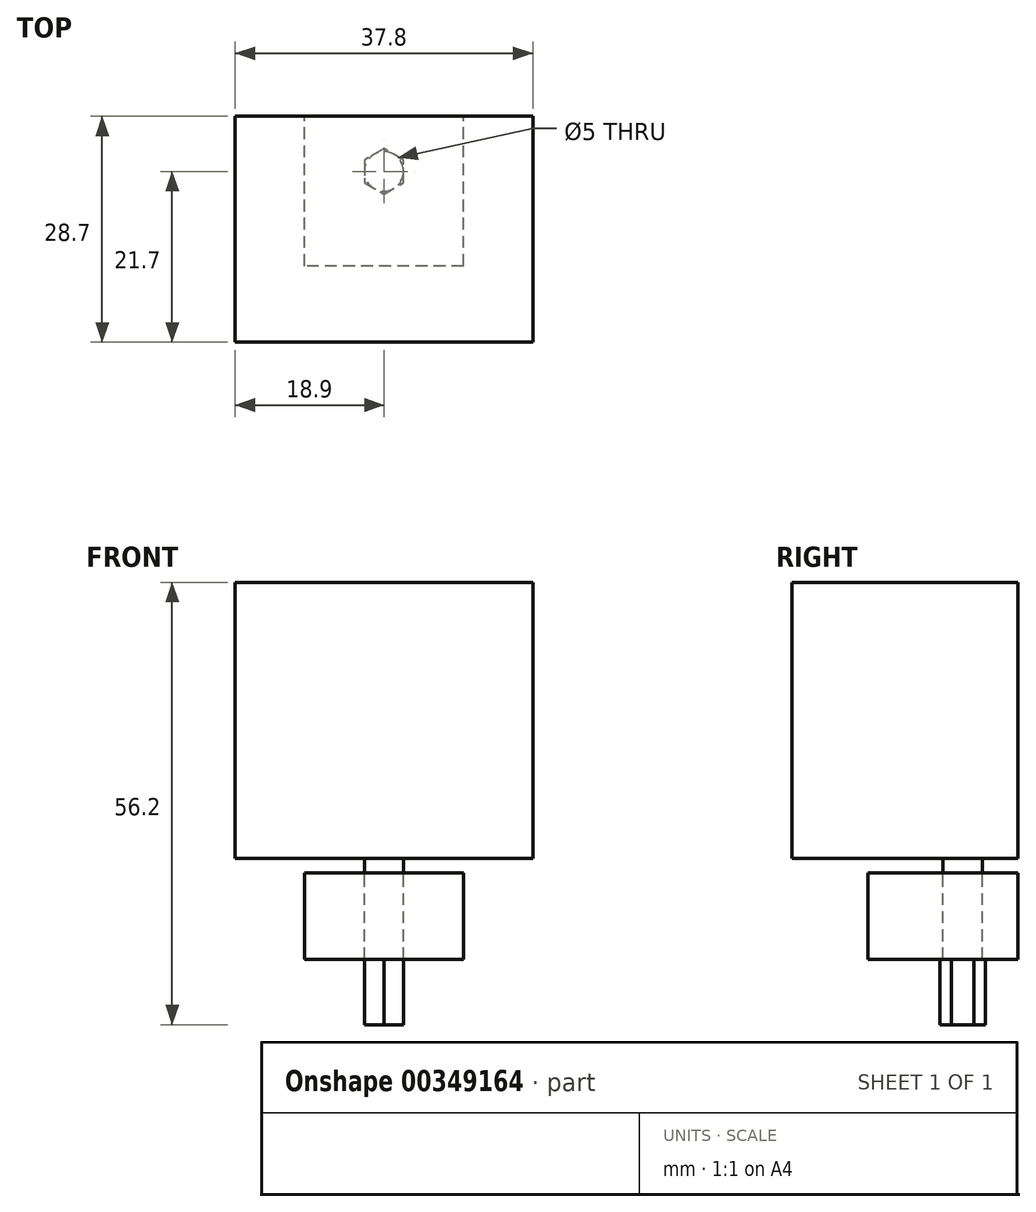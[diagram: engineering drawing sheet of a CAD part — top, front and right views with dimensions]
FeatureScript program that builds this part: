
annotation { "Feature Type Name" : "Feature", "Feature Type Description" : "" }
export const myFeature = defineFeature(function(context is Context, id is Id, definition is map)
    precondition{}
    {
        {
            var Q0;
            Q0=qCreatedBy(makeId("Top.planeOp"),FACE);
            var sketch = newSketch(context, id + "F0", { "sketchPlane" : qUnion([Q0])});
            skLineSegment(sketch, "E0.bottom", {"start": v(18.9, 14.35) * mm, "end": v(-18.9, 14.35) * mm});
            skLineSegment(sketch, "E0.top", {"start": v(18.9, -14.35) * mm, "end": v(-18.9, -14.35) * mm});
            skLineSegment(sketch, "E0.left", {"start": v(18.9, 14.35) * mm, "end": v(18.9, -14.35) * mm});
            skLineSegment(sketch, "E0.right", {"start": v(-18.9, 14.35) * mm, "end": v(-18.9, -14.35) * mm});
            skPoint(sketch, "E0.middle", {"position": v(0, 0) * mm});
            skSolve(sketch);
        }
        {
            var Q0;
            Q0 = qSketchRegion(id + "F0", true);
            extrude(context, id + "F1", {"entities" : qUnion([Q0]), "depth" : 35.1 * mm, "offsetDistance" : 25.4 * mm});
        }
        {
            var Q0;
            Q0=makeQuery(id+"F1.opExtrude","CAP_FACE",FACE,{"disambiguationData":[OSD([sQuery(id+"F0.wireOp",EDGE,"E0.bottom"),sQuery(id+"F0.wireOp",EDGE,"E0.top"),sQuery(id+"F0.wireOp",EDGE,"E0.left"),sQuery(id+"F0.wireOp",EDGE,"E0.right")])],"isStart":true});
            var sketch = newSketch(context, id + "F2", { "sketchPlane" : qUnion([Q0])});
            skCircle(sketch, "E1", {"center": v(0, -7.35) * mm, "radius": 2.5 * mm});
            skSolve(sketch);
        }
        {
            var Q0;
            Q0 = qSketchRegion(id + "F2", true);
            extrude(context, id + "F3", {"entities" : qUnion([Q0]), "operationType" : NewBodyOperationType.ADD, "depth" : 1.8 * mm, "offsetDistance" : 25 * mm});
        }
        {
            var Q0;
            Q0=makeQuery(id+"F3.opExtrude","CAP_FACE",FACE,{"disambiguationData":[OSD([sQuery(id+"F2.wireOp",EDGE,"E1")])],"isStart":false});
            var sketch = newSketch(context, id + "F4", { "sketchPlane" : qUnion([Q0])});
            skLineSegment(sketch, "E2.bottom", {"start": v(10.1, 4.65) * mm, "end": v(-10.1, 4.65) * mm});
            skLineSegment(sketch, "E2.top", {"start": v(10.1, -14.35) * mm, "end": v(-10.1, -14.35) * mm});
            skLineSegment(sketch, "E2.left", {"start": v(10.1, 4.65) * mm, "end": v(10.1, -14.35) * mm});
            skLineSegment(sketch, "E2.right", {"start": v(-10.1, 4.65) * mm, "end": v(-10.1, -14.35) * mm});
            skLineSegment(sketch, "E3", {"start": v(10.1, -7.35) * mm, "end": v(-10.1, -7.35) * mm, "construction": true});
            skCircle(sketch, "E4.0", {"center": v(0, -7.35) * mm, "radius": 2.5 * mm});
            skSolve(sketch);
        }
        {
            var Q0;
            Q0=makeQuery(id+"F4.imprint","IMPRINT",FACE,{"disambiguationData":[TD([[makeQuery(id+"F4.imprint","IMPRINT",EDGE,{"derivedFrom":sQuery(id+"F4.wireOp",EDGE,"E2.bottom")}),1.0]])]});
            extrude(context, id + "F5", {"entities" : qUnion([Q0]), "depth" : 11 * mm, "offsetDistance" : 25 * mm});
        }
        {
            var Q0;
            Q0=makeQuery(id+"F5.opExtrude","CAP_FACE",FACE,{"disambiguationData":[OSD([sQuery(id+"F4.wireOp",EDGE,"E2.bottom"),sQuery(id+"F4.wireOp",EDGE,"E2.top"),sQuery(id+"F4.wireOp",EDGE,"E2.left"),sQuery(id+"F4.wireOp",EDGE,"E2.right"),sQuery(id+"F4.wireOp",EDGE,"E4.0")])],"isStart":false});
            var sketch = newSketch(context, id + "F6", { "sketchPlane" : qUnion([Q0])});
            skCircle(sketch, "E5.0", {"center": v(0, -7.35) * mm, "radius": 2.5 * mm});
            skCircle(sketch, "E6.cCircle", {"center": v(0, -7.35) * mm, "radius": 2.5 * mm, "construction": true});
            skLineSegment(sketch, "E6.0", {"start": v(2.5, -5.9) * mm, "end": v(2.5, -8.8) * mm});
            skLineSegment(sketch, "E6.1", {"start": v(2.5, -8.8) * mm, "end": v(0, -10.24) * mm});
            skLineSegment(sketch, "E6.2", {"start": v(0, -10.24) * mm, "end": v(-2.5, -8.8) * mm});
            skLineSegment(sketch, "E6.3", {"start": v(-2.5, -8.8) * mm, "end": v(-2.5, -5.9) * mm});
            skLineSegment(sketch, "E6.4", {"start": v(-2.5, -5.9) * mm, "end": v(0, -4.46) * mm});
            skLineSegment(sketch, "E6.5", {"start": v(0, -4.46) * mm, "end": v(2.5, -5.9) * mm});
            skPoint(sketch, "E6.0.midPoint", {"position": v(2.5, -7.35) * mm});
            skSolve(sketch);
        }
        {
            var Q0;
            {var subQ0=sQuery(id+"F6.wireOp",EDGE,"E6.2");var subQ1=sQuery(id+"F6.wireOp",EDGE,"E5.0");var subQ2=makeQuery(id+"F6.imprint","INTERSECT",VERTEX,{"derivedFrom":[subQ1,subQ0]});Q0=makeQuery(id+"F6.imprint","IMPRINT",FACE,{"disambiguationData":[TD([[makeQuery(id+"F6.imprint","IMPRINT",EDGE,{"disambiguationData":[TD([[subQ2,-1.0]])],"derivedFrom":subQ1}),-1.0]])]});}
            var Q1;
            {var subQ0=sQuery(id+"F6.wireOp",EDGE,"E6.0");var subQ1=sQuery(id+"F6.wireOp",EDGE,"E5.0");var subQ2=makeQuery(id+"F6.imprint","INTERSECT",VERTEX,{"derivedFrom":[subQ1,subQ0]});Q1=makeQuery(id+"F6.imprint","IMPRINT",FACE,{"disambiguationData":[TD([[makeQuery(id+"F6.imprint","IMPRINT",EDGE,{"disambiguationData":[TD([[subQ2,1.0]])],"derivedFrom":subQ1}),-1.0]])]});}
            var Q2;
            {var subQ0=sQuery(id+"F6.wireOp",EDGE,"E6.3");var subQ1=sQuery(id+"F6.wireOp",EDGE,"E5.0");var subQ2=makeQuery(id+"F6.imprint","INTERSECT",VERTEX,{"derivedFrom":[subQ1,subQ0]});Q2=makeQuery(id+"F6.imprint","IMPRINT",FACE,{"disambiguationData":[TD([[makeQuery(id+"F6.imprint","IMPRINT",EDGE,{"disambiguationData":[TD([[subQ2,-1.0]])],"derivedFrom":subQ1}),-1.0]])]});}
            var Q3;
            {var subQ0=sQuery(id+"F6.wireOp",EDGE,"E6.5");var subQ1=sQuery(id+"F6.wireOp",EDGE,"E5.0");var subQ2=makeQuery(id+"F6.imprint","INTERSECT",VERTEX,{"derivedFrom":[subQ1,subQ0]});Q3=makeQuery(id+"F6.imprint","IMPRINT",FACE,{"disambiguationData":[TD([[makeQuery(id+"F6.imprint","IMPRINT",EDGE,{"disambiguationData":[TD([[subQ2,1.0]])],"derivedFrom":subQ1}),-1.0]])]});}
            var Q4;
            {var subQ0=sQuery(id+"F6.wireOp",EDGE,"E6.4");var subQ1=sQuery(id+"F6.wireOp",EDGE,"E5.0");var subQ2=makeQuery(id+"F6.imprint","INTERSECT",VERTEX,{"derivedFrom":[subQ1,subQ0]});Q4=makeQuery(id+"F6.imprint","IMPRINT",FACE,{"disambiguationData":[TD([[makeQuery(id+"F6.imprint","IMPRINT",EDGE,{"disambiguationData":[TD([[subQ2,-1.0]])],"derivedFrom":subQ1}),-1.0]])]});}
            var Q5;
            {var subQ0=sQuery(id+"F6.wireOp",EDGE,"E5.0");var subQ4=makeQuery(id+"F6.imprint","INTERSECT",VERTEX,{"derivedFrom":[subQ0,sQuery(id+"F6.wireOp",EDGE,"E6.5")]});Q5=makeQuery(id+"F6.imprint","IMPRINT",FACE,{"disambiguationData":[TD([[makeQuery(id+"F6.imprint","IMPRINT",EDGE,{"disambiguationData":[TD([[subQ4,1.0]])],"derivedFrom":subQ0}),1.0]])]});}
            var Q6;
            {var subQ0=sQuery(id+"F6.wireOp",EDGE,"E6.5");var subQ1=sQuery(id+"F6.wireOp",EDGE,"E5.0");var subQ2=makeQuery(id+"F6.imprint","INTERSECT",VERTEX,{"derivedFrom":[subQ1,subQ0]});Q6=makeQuery(id+"F6.imprint","IMPRINT",FACE,{"disambiguationData":[TD([[makeQuery(id+"F6.imprint","IMPRINT",EDGE,{"disambiguationData":[TD([[subQ2,-1.0]])],"derivedFrom":subQ1}),-1.0]])]});}
            extrude(context, id + "F7", {"entities" : qUnion([Q0, Q1, Q2, Q3, Q4, Q5, Q6]), "depth" : 8.3 * mm, "offsetDistance" : 25 * mm});
        }
        {
            var Q0;
            Q0=makeQuery(id+"F6.imprint","IMPRINT",FACE,{"disambiguationData":[TD([[makeQuery(id+"F6.imprint","IMPRINT",EDGE,{"derivedFrom":makeQuery(id+"F5.opExtrude","CAP_EDGE",EDGE,{"disambiguationData":[OSD([sQuery(id+"F4.wireOp",EDGE,"E2.bottom")])],"isStart":false})}),1.0]])]});
            cPlane(context, id + "F8", {"entities" : qUnion([Q0]), "cplaneType" : CPlaneType.OFFSET, "offset" : 1 * mm, "width" : 150 * mm, "height" : 150 * mm});
        }
        {
            var Q0;
            Q0=qCreatedBy(id+"F8.planeOp",FACE);
            var sketch = newSketch(context, id + "F9", { "sketchPlane" : qUnion([Q0])});
            skCircle(sketch, "E7.0", {"center": v(0, -7.35) * mm, "radius": 2.5 * mm, "construction": true});
            skCircle(sketch, "E8.0", {"center": v(0, -7.35) * mm, "radius": 3.5 * mm});
            skSolve(sketch);
        }
        {
            var Q0;
            Q0=sQuery(id+"F9.wireOp",VERTEX,"E8.0.center");
            var Q1;
            Q1=makeQuery(id+"F5.opExtrude","SWEPT_FACE",FACE,{"disambiguationData":[OSD([sQuery(id+"F4.wireOp",EDGE,"E2.bottom")])]});
            cPlane(context, id + "F10", {"entities" : qUnion([Q0, Q1]), "cplaneType" : CPlaneType.PLANE_POINT, "offset" : 25 * mm, "width" : 150 * mm, "height" : 150 * mm});
        }
    });
